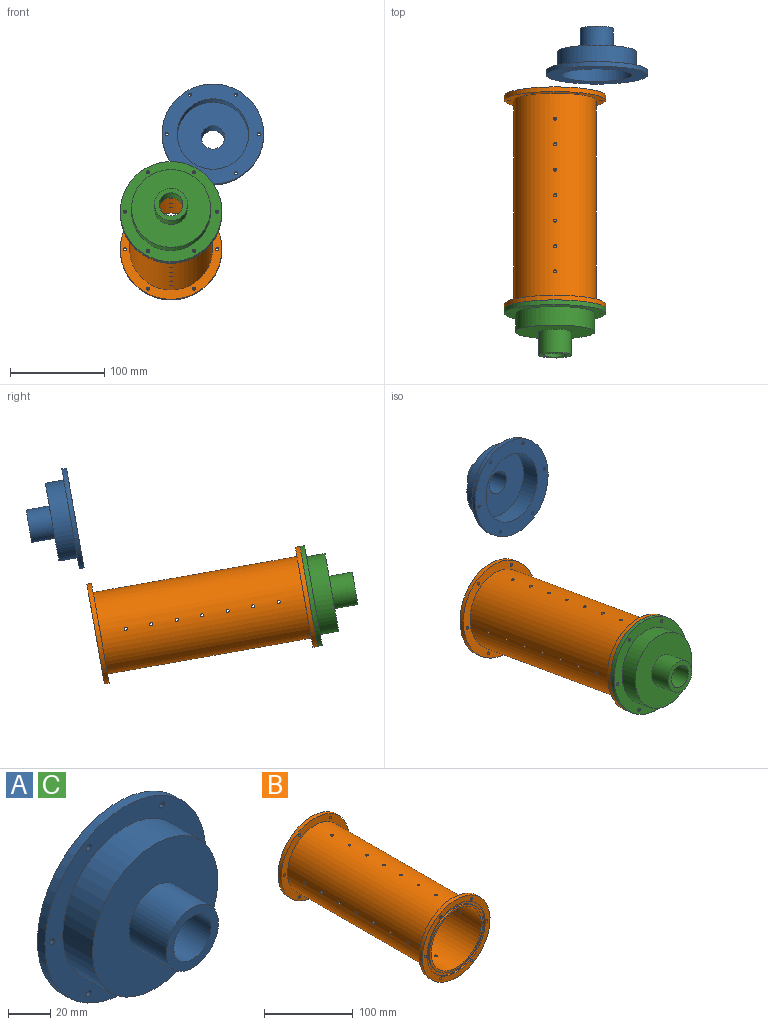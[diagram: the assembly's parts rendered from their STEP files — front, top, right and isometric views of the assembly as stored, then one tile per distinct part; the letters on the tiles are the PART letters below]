
ASSEMBLY  parts=3 mates=2
PART A: 16 faces, bbox 108x50x108 mm
  f0: plane 108x108mm, normal (0,1,0), area 4573.1mm2, adj f1,f3,f4,f5,f6,f7,f8,f9
  f1: cylinder r=38mm len=76mm, axis (0,1,0), area 5014mm2, adj f0,f11
  f2: plane 108x108mm, normal (0,-1,0), area 3567.8mm2, adj f3,f4,f5,f6,f7,f8,f9,f10
  f3: cylinder r=54mm len=108mm, axis (0,-1,0), area 1696.5mm2, adj f0,f2
  f4: cylinder r=1.65mm len=5mm, axis (0,1,0), area 51.8mm2, adj f0,f2
  f5: cylinder r=1.65mm len=5mm, axis (0,1,0), area 51.8mm2, adj f0,f2
  f6: cylinder r=1.65mm len=5mm, axis (0,1,0), area 51.8mm2, adj f0,f2
  f7: cylinder r=1.65mm len=5mm, axis (0,1,0), area 51.8mm2, adj f0,f2
  f8: cylinder r=1.65mm len=5mm, axis (0,1,0), area 51.8mm2, adj f0,f2
  f9: cylinder r=1.65mm len=5mm, axis (0,1,0), area 51.8mm2, adj f0,f2
  f10: cylinder r=42mm len=84mm, axis (0,1,0), area 5277.9mm2, adj f2,f13
  f11: plane 76x76mm, normal (0,1,0), area 4045.6mm2, adj f1,f12
  f12: cylinder r=12.5mm len=29mm, axis (0,1,0), area 2277.7mm2, adj f11,f14
  f13: plane 84x84mm, normal (0,-1,0), area 4579.7mm2, adj f10,f15
  f14: plane 35x35mm, normal (0,-1,0), area 471.2mm2, adj f12,f15
  f15: cylinder r=17.5mm len=35mm, axis (0,1,0), area 2748.9mm2, adj f13,f14
PART B: 56 faces, bbox 108x230x108 mm
  f0: cylinder r=54mm len=108mm, axis (0,-1,0), area 1696.5mm2, adj f7,f51
  f1: cylinder r=40mm len=230mm, axis (0,-1,0), area 57563.8mm2, adj f3,f23,f24,f25,f26,f27,f28,f29
  f2: cylinder r=44mm len=220mm, axis (0,-1,0), area 60579.6mm2, adj f6,f7,f23,f24,f25,f26,f27,f28
  f3: plane 85x85mm, normal (0,1,0), area 648mm2, adj f1,f20
  f4: plane 108x108mm, normal (0,1,0), area 2375mm2, adj f5,f14,f15,f16,f17,f18,f19,f21
  f5: cylinder r=54mm len=108mm, axis (0,-1,0), area 1696.5mm2, adj f4,f6
  f6: plane 108x108mm, normal (0,-1,0), area 3027.4mm2, adj f2,f5,f14,f15,f16,f17,f18,f19
  f7: plane 108x108mm, normal (0,1,0), area 3027.4mm2, adj f0,f2,f8,f9,f10,f11,f12,f13
  f8: cylinder r=1.65mm len=5mm, axis (0,-1,0), area 51.8mm2, adj f7,f51
  f9: cylinder r=1.65mm len=5mm, axis (0,-1,0), area 51.8mm2, adj f7,f51
  f10: cylinder r=1.65mm len=5mm, axis (0,-1,0), area 51.8mm2, adj f7,f51
  f11: cylinder r=1.65mm len=5mm, axis (0,-1,0), area 51.8mm2, adj f7,f51
  f12: cylinder r=1.65mm len=5mm, axis (0,-1,0), area 51.8mm2, adj f7,f51
  f13: cylinder r=1.65mm len=5mm, axis (0,-1,0), area 51.8mm2, adj f7,f51
  f14: cylinder r=1.65mm len=5mm, axis (0,-1,0), area 51.8mm2, adj f4,f6
  f15: cylinder r=1.65mm len=5mm, axis (0,-1,0), area 51.8mm2, adj f4,f6
  f16: cylinder r=1.65mm len=5mm, axis (0,-1,0), area 51.8mm2, adj f4,f6
  f17: cylinder r=1.65mm len=5mm, axis (0,-1,0), area 51.8mm2, adj f4,f6
  f18: cylinder r=1.65mm len=5mm, axis (0,-1,0), area 51.8mm2, adj f4,f6
  f19: cylinder r=1.65mm len=5mm, axis (0,-1,0), area 51.8mm2, adj f4,f6
  f20: cylinder r=42.5mm len=85mm, axis (0,1,0), area 526.1mm2, adj f3,f22
  f21: cylinder r=46.3mm len=92.6mm, axis (0,1,0), area 573.1mm2, adj f4,f22
  f22: plane 92.6x92.6mm, normal (0,1,0), area 1060.1mm2, adj f20,f21
  f23: cylinder r=1.65mm len=4.03mm, axis (1,0,0), area 41.5mm2, adj f1,f2
  f24: cylinder r=1.65mm len=4.03mm, axis (1,0,0), area 41.5mm2, adj f1,f2
  f25: cylinder r=1.65mm len=4.03mm, axis (1,0,0), area 41.5mm2, adj f1,f2
  f26: cylinder r=1.65mm len=4.03mm, axis (1,0,0), area 41.5mm2, adj f1,f2
  f27: cylinder r=1.65mm len=4.03mm, axis (1,0,0), area 41.5mm2, adj f1,f2
  f28: cylinder r=1.65mm len=4.03mm, axis (1,0,0), area 41.5mm2, adj f1,f2
  f29: cylinder r=1.65mm len=4.03mm, axis (1,0,0), area 41.5mm2, adj f1,f2
  f30: cylinder r=1.65mm len=4.03mm, axis (-1,0,0), area 41.5mm2, adj f1,f2
  f31: cylinder r=1.65mm len=4.03mm, axis (-1,0,0), area 41.5mm2, adj f1,f2
  f32: cylinder r=1.65mm len=4.03mm, axis (-1,0,0), area 41.5mm2, adj f1,f2
  f33: cylinder r=1.65mm len=4.03mm, axis (-1,0,0), area 41.5mm2, adj f1,f2
  f34: cylinder r=1.65mm len=4.03mm, axis (-1,0,0), area 41.5mm2, adj f1,f2
  f35: cylinder r=1.65mm len=4.03mm, axis (-1,0,0), area 41.5mm2, adj f1,f2
  f36: cylinder r=1.65mm len=4.03mm, axis (-1,0,0), area 41.5mm2, adj f1,f2
  f37: cylinder r=1.65mm len=4.03mm, axis (0,0,1), area 41.5mm2, adj f1,f2
  f38: cylinder r=1.65mm len=4.03mm, axis (0,0,1), area 41.5mm2, adj f1,f2
  f39: cylinder r=1.65mm len=4.03mm, axis (0,0,1), area 41.5mm2, adj f1,f2
  f40: cylinder r=1.65mm len=4.03mm, axis (0,0,1), area 41.5mm2, adj f1,f2
  f41: cylinder r=1.65mm len=4.03mm, axis (0,0,1), area 41.5mm2, adj f1,f2
  f42: cylinder r=1.65mm len=4.03mm, axis (0,0,1), area 41.5mm2, adj f1,f2
  f43: cylinder r=1.65mm len=4.03mm, axis (0,0,1), area 41.5mm2, adj f1,f2
  f44: cylinder r=1.65mm len=4.03mm, axis (0,0,-1), area 41.5mm2, adj f1,f2
  f45: cylinder r=1.65mm len=4.03mm, axis (0,0,-1), area 41.5mm2, adj f1,f2
  f46: cylinder r=1.65mm len=4.03mm, axis (0,0,-1), area 41.5mm2, adj f1,f2
  f47: cylinder r=1.65mm len=4.03mm, axis (0,0,-1), area 41.5mm2, adj f1,f2
  f48: cylinder r=1.65mm len=4.03mm, axis (0,0,-1), area 41.5mm2, adj f1,f2
  f49: cylinder r=1.65mm len=4.03mm, axis (0,0,-1), area 41.5mm2, adj f1,f2
  f50: cylinder r=1.65mm len=4.03mm, axis (0,0,-1), area 41.5mm2, adj f1,f2
  f51: plane 108x108mm, normal (0,-1,0), area 2375mm2, adj f0,f8,f9,f10,f11,f12,f13,f53
  f52: plane 85x85mm, normal (0,-1,0), area 648mm2, adj f1,f55
  f53: cylinder r=46.3mm len=92.6mm, axis (0,-1,0), area 573.1mm2, adj f51,f54
  f54: plane 92.6x92.6mm, normal (0,-1,0), area 1060.1mm2, adj f53,f55
  f55: cylinder r=42.5mm len=85mm, axis (0,-1,0), area 526.1mm2, adj f52,f54
PART C: same geometry as A
PLACE A rot(axis=(1,0,0),170deg) t=(-193.64,201.82,-315.93)mm
PLACE B rot(axis=(0,-1,0.09),180deg) t=(-238.14,-46.43,-399.32)mm
PLACE C rot(axis=(0,-1,0.09),180deg) t=(-238.14,-46.43,-399.32)mm
MATE fastened B.f0 <-> C.f3  axis (0,-0.98,0.17) through (-238.14,-46.43,-399.32)mm
MATE planar A.f3 <-> B.f21  axis (0,-0.98,0.17) through (-193.64,201.82,-315.93)mm
